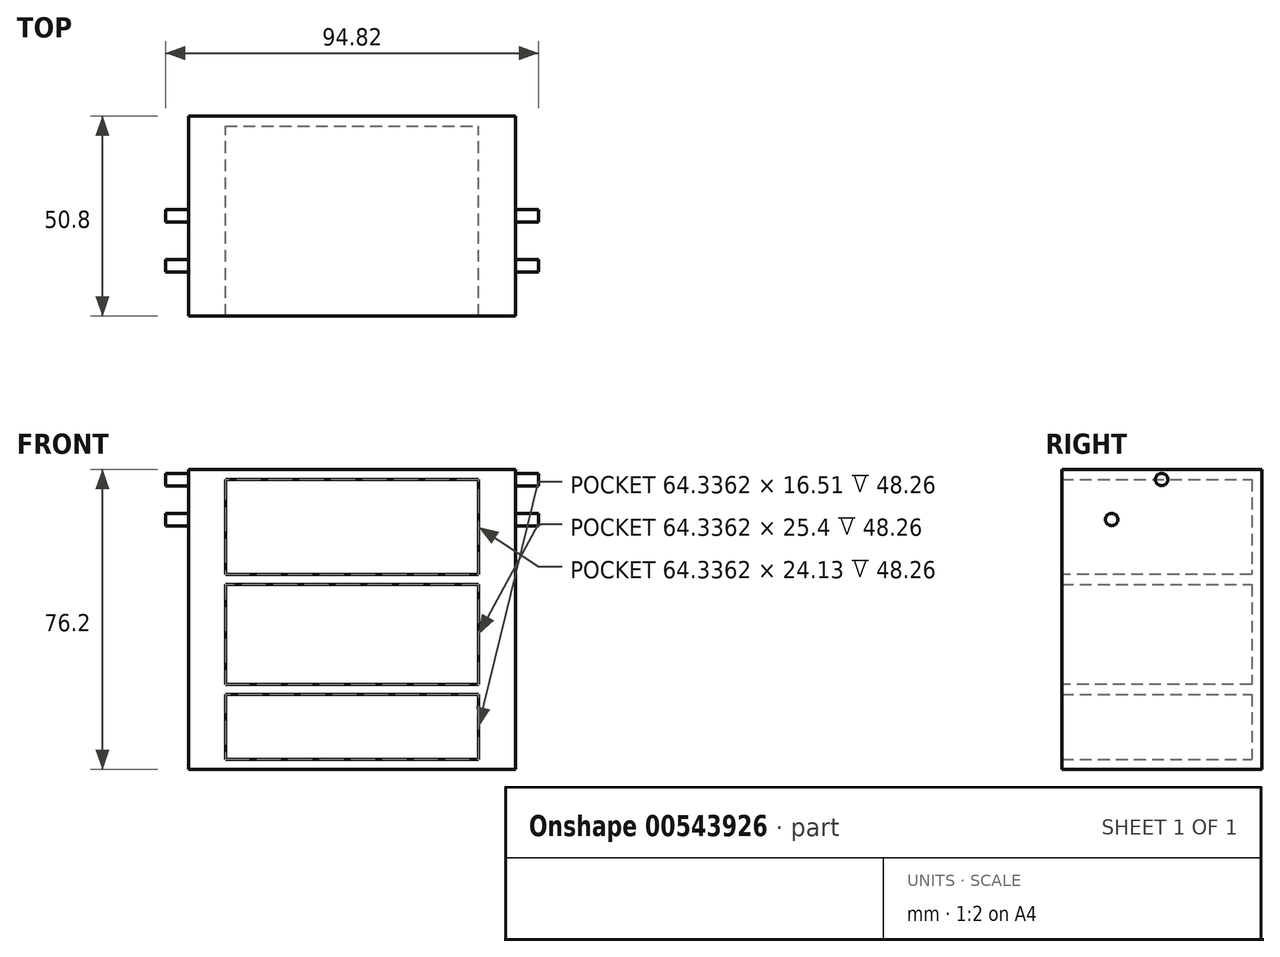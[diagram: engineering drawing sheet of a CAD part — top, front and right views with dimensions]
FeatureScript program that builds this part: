
annotation { "Feature Type Name" : "Feature", "Feature Type Description" : "" }
export const myFeature = defineFeature(function(context is Context, id is Id, definition is map)
    precondition{}
    {
        {
            var Q0;
            Q0=qCreatedBy(makeId("Top.planeOp"),FACE);
            var sketch = newSketch(context, id + "F0", { "sketchPlane" : qUnion([Q0])});
            skLineSegment(sketch, "E0.bottom", {"start": v(-37.25, -35.66) * mm, "end": v(33.87, -35.66) * mm});
            skLineSegment(sketch, "E0.top", {"start": v(-37.25, 15.14) * mm, "end": v(33.87, 15.14) * mm});
            skLineSegment(sketch, "E0.left", {"start": v(-37.25, -35.66) * mm, "end": v(-37.25, 15.14) * mm});
            skLineSegment(sketch, "E0.right", {"start": v(33.87, -35.66) * mm, "end": v(33.87, 15.14) * mm});
            skSolve(sketch);
        }
        {
            var Q0;
            Q0 = qSketchRegion(id + "F0", true);
            extrude(context, id + "F1", {"entities" : qUnion([Q0]), "depth" : 76.2 * mm, "offsetDistance" : 25.4 * mm});
        }
        {
            var Q0;
            Q0=makeQuery(id+"F1.opExtrude","SWEPT_FACE",FACE,{"disambiguationData":[OSD([sQuery(id+"F0.wireOp",EDGE,"E0.bottom")])]});
            var sketch = newSketch(context, id + "F2", { "sketchPlane" : qUnion([Q0])});
            skLineSegment(sketch, "E1", {"start": v(-1.69, 19.05) * mm, "end": v(-37.25, 19.05) * mm});
            skLineSegment(sketch, "E2.bottom", {"start": v(-37.25, 19.05) * mm, "end": v(33.87, 19.05) * mm});
            skLineSegment(sketch, "E2.top", {"start": v(-37.25, 21.6) * mm, "end": v(33.87, 21.6) * mm});
            skLineSegment(sketch, "E2.left", {"start": v(-37.25, 19.05) * mm, "end": v(-37.25, 21.6) * mm});
            skLineSegment(sketch, "E2.right", {"start": v(33.87, 19.05) * mm, "end": v(33.87, 21.6) * mm});
            skLineSegment(sketch, "E3", {"start": v(33.87, 21.6) * mm, "end": v(-1.69, 21.6) * mm});
            skLineSegment(sketch, "E4", {"start": v(-1.69, 47) * mm, "end": v(-37.25, 47) * mm});
            skLineSegment(sketch, "E5.bottom", {"start": v(-37.25, 47) * mm, "end": v(33.87, 47) * mm});
            skLineSegment(sketch, "E5.top", {"start": v(-37.25, 49.53) * mm, "end": v(33.87, 49.53) * mm});
            skLineSegment(sketch, "E5.left", {"start": v(-37.25, 47) * mm, "end": v(-37.25, 49.53) * mm});
            skLineSegment(sketch, "E5.right", {"start": v(33.87, 47) * mm, "end": v(33.87, 49.53) * mm});
            skSolve(sketch);
        }
        {
            var Q0;
            Q0=makeQuery(id+"F1.opExtrude","SWEPT_FACE",FACE,{"disambiguationData":[OSD([sQuery(id+"F0.wireOp",EDGE,"E0.bottom")])]});
            shell(context, id + "F3", {"entities" : qUnion([Q0]), "thickness" : 2.54 * mm});
        }
        {
            var Q0;
            Q0=makeQuery(id+"F2.imprint","IMPRINT",FACE,{"disambiguationData":[TD([[makeQuery(id+"F2.imprint","IMPRINT",EDGE,{"derivedFrom":sQuery(id+"F2.wireOp",EDGE,"E5.top")}),-1.0]])]});
            extrude(context, id + "F4", {"entities" : qUnion([Q0]), "operationType" : NewBodyOperationType.ADD, "oppositeDirection" : true, "depth" : 50.8 * mm, "offsetDistance" : 25.4 * mm});
        }
        {
            var Q0;
            Q0=makeQuery(id+"F2.imprint","IMPRINT",FACE,{"disambiguationData":[TD([[makeQuery(id+"F2.imprint","IMPRINT",EDGE,{"derivedFrom":sQuery(id+"F2.wireOp",EDGE,"E2.top")}),-1.0]])]});
            extrude(context, id + "F5", {"entities" : qUnion([Q0]), "operationType" : NewBodyOperationType.ADD, "oppositeDirection" : true, "depth" : 50.8 * mm, "offsetDistance" : 25.4 * mm});
        }
        {
            var Q0;
            Q0=makeQuery(id+"F1.opExtrude","SWEPT_FACE",FACE,{"disambiguationData":[OSD([sQuery(id+"F0.wireOp",EDGE,"E0.left")])]});
            var sketch = newSketch(context, id + "F6", { "sketchPlane" : qUnion([Q0])});
            skLineSegment(sketch, "E6", {"start": v(35.66, 0) * mm, "end": v(22.96, 0) * mm});
            skLineSegment(sketch, "E7", {"start": v(22.96, 0) * mm, "end": v(22.96, 63.5) * mm});
            skLineSegment(sketch, "E8", {"start": v(22.96, 63.5) * mm, "end": v(10.26, 63.5) * mm});
            skLineSegment(sketch, "E9", {"start": v(10.26, 63.5) * mm, "end": v(10.26, 73.66) * mm});
            skCircle(sketch, "E10", {"center": v(22.96, 63.5) * mm, "radius": 1.59 * mm});
            skCircle(sketch, "E11", {"center": v(10.26, 73.66) * mm, "radius": 1.59 * mm});
            skSolve(sketch);
        }
        {
            var Q0;
            Q0=makeQuery(id+"F6.imprint","IMPRINT",FACE,{"disambiguationData":[TD([[makeQuery(id+"F6.imprint","IMPRINT",EDGE,{"derivedFrom":sQuery(id+"F6.wireOp",EDGE,"E11")}),1.0]])]});
            extrude(context, id + "F7", {"entities" : qUnion([Q0]), "operationType" : NewBodyOperationType.ADD, "depth" : 12.7 * mm, "offsetDistance" : 25.4 * mm});
        }
        {
            var Q0;
            {var subQ0=sQuery(id+"F6.wireOp",EDGE,"E8");var subQ1=sQuery(id+"F6.wireOp",EDGE,"E7");var subQ2=makeQuery(id+"F6.imprint","INTERSECT",VERTEX,{"derivedFrom":[subQ1,subQ0]});Q0=makeQuery(id+"F6.imprint","IMPRINT",FACE,{"disambiguationData":[TD([[makeQuery(id+"F6.imprint","IMPRINT",EDGE,{"disambiguationData":[TD([[subQ2,1.0]])],"derivedFrom":subQ1}),-1.0]])]});}
            extrude(context, id + "F8", {"entities" : qUnion([Q0]), "operationType" : NewBodyOperationType.ADD, "depth" : 12.7 * mm, "offsetDistance" : 25.4 * mm});
        }
        {
            var Q0;
            {var subQ0=sQuery(id+"F6.wireOp",EDGE,"E8");var subQ1=sQuery(id+"F6.wireOp",EDGE,"E7");var subQ2=makeQuery(id+"F6.imprint","INTERSECT",VERTEX,{"derivedFrom":[subQ1,subQ0]});Q0=makeQuery(id+"F6.imprint","IMPRINT",FACE,{"disambiguationData":[TD([[makeQuery(id+"F6.imprint","IMPRINT",EDGE,{"disambiguationData":[TD([[subQ2,1.0]])],"derivedFrom":subQ1}),1.0]])]});}
            extrude(context, id + "F9", {"entities" : qUnion([Q0]), "operationType" : NewBodyOperationType.ADD, "depth" : 12.7 * mm, "offsetDistance" : 25.4 * mm});
        }
        {
            var Q0;
            Q0=qCreatedBy(makeId("Right.planeOp"),FACE);
            cPlane(context, id + "F10", {"entities" : qUnion([Q0]), "cplaneType" : CPlaneType.OFFSET, "offset" : 2.54 * mm, "oppositeDirection" : true, "width" : 152.4 * mm, "height" : 152.4 * mm});
        }
        {
            var Q0;
            Q0=makeQuery(id+"F1.opExtrude","SWEPT_BODY",BODY,{"disambiguationData":[OSD([sQuery(id+"F0.wireOp",EDGE,"E0.bottom"),sQuery(id+"F0.wireOp",EDGE,"E0.top"),sQuery(id+"F0.wireOp",EDGE,"E0.left"),sQuery(id+"F0.wireOp",EDGE,"E0.right")])]});
            var Q1;
            Q1=qCreatedBy(id+"F10.planeOp",FACE);
            mirror(context, id + "F11", {"operationType" : NewBodyOperationType.ADD, "entities" : qUnion([Q0]), "mirrorPlane" : qUnion([Q1])});
        }
        {
            var Q0;
            Q0=makeQuery(id+"F11.opPattern","COPY",FACE,{"derivedFrom":makeQuery(id+"F1.opExtrude","SWEPT_FACE",FACE,{"disambiguationData":[OSD([sQuery(id+"F0.wireOp",EDGE,"E0.right")])]}),"instanceName":"1"});
            extrude(context, id + "F12", {"entities" : qUnion([Q0]), "operationType" : NewBodyOperationType.ADD, "depth" : 5.08 * mm, "offsetDistance" : 25.4 * mm});
        }
        {
            var Q0;
            Q0=makeQuery(id+"F1.opExtrude","SWEPT_FACE",FACE,{"disambiguationData":[OSD([sQuery(id+"F0.wireOp",EDGE,"E0.right")])]});
            extrude(context, id + "F13", {"entities" : qUnion([Q0]), "operationType" : NewBodyOperationType.ADD, "depth" : 5.08 * mm, "offsetDistance" : 25.4 * mm});
        }
    });
